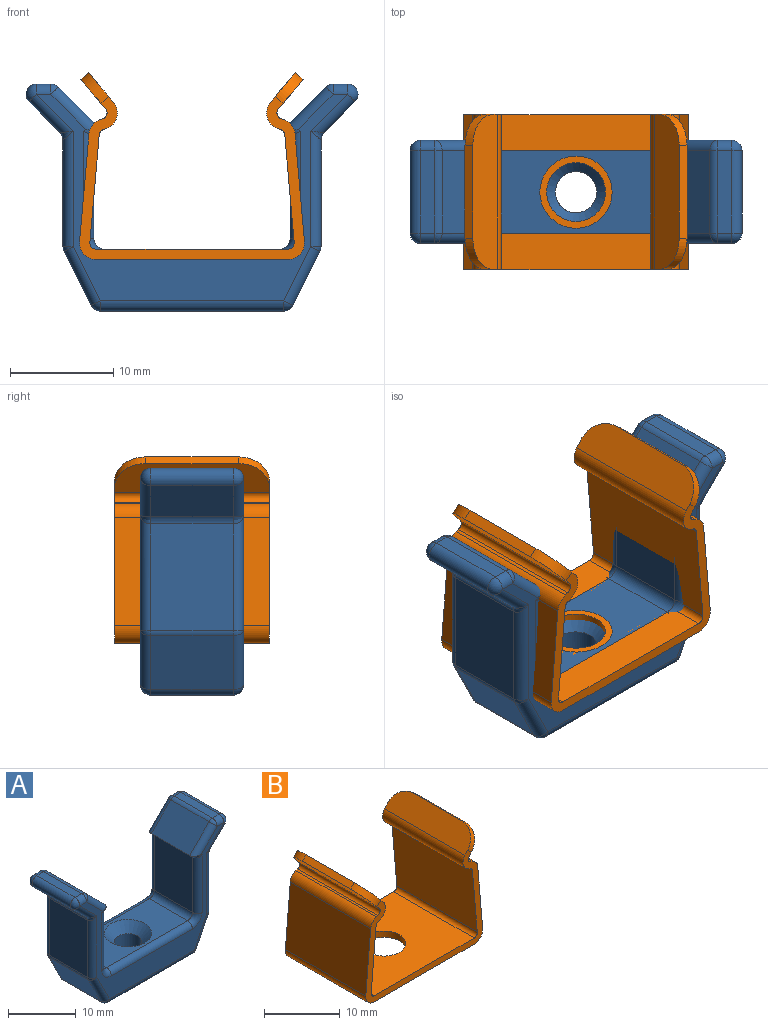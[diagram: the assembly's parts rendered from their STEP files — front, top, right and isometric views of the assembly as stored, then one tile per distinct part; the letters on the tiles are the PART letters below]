
ASSEMBLY  parts=2 mates=1
PART A: 88 faces, bbox 32.2x10x22 mm
  f0: plane 17x8mm, normal (0,0,1), area 97.5mm2, adj f27,f36,f37,f38,f69
  f1: plane 10x8mm, normal (1,0,0), area 80mm2, adj f2,f26,f27,f28
  f2: plane 8x0.62mm, normal (0.71,0,-0.71), area 7mm2, adj f1,f3,f22,f23
  f3: plane 8x4.09mm, normal (0.71,0,0.71), area 46.2mm2, adj f2,f18,f19,f20
  f4: plane 8x1.41mm, normal (0,0,1), area 11.3mm2, adj f20,f25,f29,f30
  f5: plane 8x3mm, normal (-0.71,0,-0.71), area 33.9mm2, adj f30,f35,f39,f83
  f6: plane 10.35x8mm, normal (-1,0,0), area 82.8mm2, adj f40,f43,f77,f83
  f7: plane 8x5.24mm, normal (-0.89,0,-0.45), area 46.8mm2, adj f44,f47,f77,f80
  f8: plane 17.76x8mm, normal (0,0,-1), area 129.5mm2, adj f48,f51,f68,f71,f80
  f9: plane 8x5.24mm, normal (0.89,0,-0.45), area 46.8mm2, adj f52,f56,f71,f74
  f10: plane 10.35x8mm, normal (1,0,0), area 82.8mm2, adj f57,f60,f74,f86
  f11: plane 8x3mm, normal (0.71,0,-0.71), area 33.9mm2, adj f61,f64,f67,f86
  f12: plane 8x1.41mm, normal (0,0,1), area 11.3mm2, adj f54,f62,f63,f67
  f13: plane 8x4.09mm, normal (-0.71,0,0.71), area 46.2mm2, adj f14,f53,f54,f55
  f14: plane 8x0.62mm, normal (-0.71,0,-0.71), area 7mm2, adj f13,f15,f49,f50
  f15: plane 10x8mm, normal (-1,0,0), area 80mm2, adj f14,f37,f45,f46
  f16: plane 30.17x20mm, normal (0,-1,0), area 114.9mm2, adj f18,f22,f25,f26,f32,f35,f36,f40
  f17: plane 30.17x20mm, normal (0,1,0), area 114.9mm2, adj f19,f23,f28,f29,f33,f38,f39,f42
  f18: cylinder r=1mm len=4.79mm, axis (0.71,0,-0.71), area 8.5mm2, adj f3,f16,f21,f22
  f19: cylinder r=1mm len=4.79mm, axis (-0.71,0,0.71), area 8.5mm2, adj f3,f17,f23,f24
  f20: cylinder r=1mm len=8mm, axis (0,1,0), area 6.3mm2, adj f3,f4,f21,f24
  f21: sphere r=1mm, area 0.8mm2, adj f18,f20,f25
  f22: cylinder r=1mm len=1.62mm, axis (-0.71,0,-0.71), area 1mm2, adj f2,f16,f18,f26
  f23: cylinder r=1mm len=1.62mm, axis (0.71,0,0.71), area 1mm2, adj f2,f17,f19,f28
  f24: sphere r=1mm, area 0.8mm2, adj f19,f20,f29
  f25: cylinder r=1mm len=1.41mm, axis (1,0,0), area 2.2mm2, adj f4,f16,f21,f31
  f26: cylinder r=1mm len=10.41mm, axis (0,0,-1), area 15.9mm2, adj f1,f16,f22,f32
  f27: cylinder r=1mm len=8mm, axis (0,1,0), area 12.6mm2, adj f0,f1,f32,f33
  f28: cylinder r=1mm len=10.41mm, axis (0,0,1), area 15.9mm2, adj f1,f17,f23,f33
  f29: cylinder r=1mm len=1.41mm, axis (-1,0,0), area 2.2mm2, adj f4,f17,f24,f34
  f30: cylinder r=1mm len=8mm, axis (0,1,0), area 18.8mm2, adj f4,f5,f31,f34
  f31: sphere r=1mm, area 2.4mm2, adj f25,f30,f35
  f32: torus R=2mm, axis (0,-1,0), area 3.4mm2, adj f16,f26,f27,f36
  f33: torus R=2mm, axis (0,-1,0), area 3.4mm2, adj f17,f27,f28,f38
  f34: sphere r=1mm, area 2.4mm2, adj f29,f30,f39
  f35: cylinder r=1mm len=4.29mm, axis (-0.71,0,0.71), area 7.1mm2, adj f5,f16,f31,f84
  f36: cylinder r=1mm len=17mm, axis (1,0,0), area 26.7mm2, adj f0,f16,f32,f41
  f37: cylinder r=1mm len=8mm, axis (0,-1,0), area 12.6mm2, adj f0,f15,f41,f42
  f38: cylinder r=1mm len=17mm, axis (-1,0,0), area 26.7mm2, adj f0,f17,f33,f42
  f39: cylinder r=1mm len=4.29mm, axis (0.71,0,-0.71), area 7.1mm2, adj f5,f17,f34,f82
  f40: cylinder r=1mm len=11.18mm, axis (0,0,1), area 16.7mm2, adj f6,f16,f78,f84
  f41: torus R=2mm, axis (0,-1,0), area 3.4mm2, adj f16,f36,f37,f45
  f42: torus R=2mm, axis (0,-1,0), area 3.4mm2, adj f17,f37,f38,f46
  f43: cylinder r=1mm len=11.18mm, axis (0,0,-1), area 16.7mm2, adj f6,f17,f76,f82
  f44: cylinder r=1mm len=5.68mm, axis (-0.45,0,0.89), area 9.2mm2, adj f7,f16,f78,f81
  f45: cylinder r=1mm len=10.41mm, axis (0,0,1), area 15.9mm2, adj f15,f16,f41,f49
  f46: cylinder r=1mm len=10.41mm, axis (0,0,-1), area 15.9mm2, adj f15,f17,f42,f50
  f47: cylinder r=1mm len=5.68mm, axis (0.45,0,-0.89), area 9.2mm2, adj f7,f17,f76,f79
  f48: cylinder r=1mm len=17.76mm, axis (-1,0,0), area 27.9mm2, adj f8,f16,f72,f81
  f49: cylinder r=1mm len=1.62mm, axis (-0.71,0,0.71), area 1mm2, adj f14,f16,f45,f53
  f50: cylinder r=1mm len=1.62mm, axis (0.71,0,-0.71), area 1mm2, adj f14,f17,f46,f55
  f51: cylinder r=1mm len=17.76mm, axis (1,0,0), area 27.9mm2, adj f8,f17,f70,f79
  f52: cylinder r=1mm len=5.68mm, axis (-0.45,0,-0.89), area 9.2mm2, adj f9,f16,f72,f75
  f53: cylinder r=1mm len=4.79mm, axis (0.71,0,0.71), area 8.5mm2, adj f13,f16,f49,f58
  f54: cylinder r=1mm len=8mm, axis (0,1,0), area 6.3mm2, adj f12,f13,f58,f59
  f55: cylinder r=1mm len=4.79mm, axis (-0.71,0,-0.71), area 8.5mm2, adj f13,f17,f50,f59
  f56: cylinder r=1mm len=5.68mm, axis (0.45,0,0.89), area 9.2mm2, adj f9,f17,f70,f73
  f57: cylinder r=1mm len=11.18mm, axis (0,0,-1), area 16.7mm2, adj f10,f16,f75,f87
  f58: sphere r=1mm, area 0.8mm2, adj f53,f54,f62
  f59: sphere r=1mm, area 0.8mm2, adj f54,f55,f63
  f60: cylinder r=1mm len=11.18mm, axis (0,0,1), area 16.7mm2, adj f10,f17,f73,f85
  f61: cylinder r=1mm len=4.29mm, axis (-0.71,0,-0.71), area 7.1mm2, adj f11,f16,f65,f87
  f62: cylinder r=1mm len=1.41mm, axis (1,0,0), area 2.2mm2, adj f12,f16,f58,f65
  f63: cylinder r=1mm len=1.41mm, axis (-1,0,0), area 2.2mm2, adj f12,f17,f59,f66
  f64: cylinder r=1mm len=4.29mm, axis (0.71,0,0.71), area 7.1mm2, adj f11,f17,f66,f85
  f65: sphere r=1mm, area 2.4mm2, adj f61,f62,f67
  f66: sphere r=1mm, area 2.4mm2, adj f63,f64,f67
  f67: cylinder r=1mm len=8mm, axis (0,1,0), area 18.8mm2, adj f11,f12,f65,f66
  f68: cylinder r=2mm len=4.5mm, axis (0,0,1), area 56.5mm2, adj f8,f69
  f69: cone r=2mm half-angle=45deg, axis (0,0,1), area 36.7mm2, adj f0,f68
  f70: sphere r=1mm, area 1.1mm2, adj f51,f56,f71
  f71: cylinder r=1mm len=8mm, axis (0,-1,0), area 8.9mm2, adj f8,f9,f70,f72
  f72: sphere r=1mm, area 1.1mm2, adj f48,f52,f71
  f73: sphere r=1mm, area 0.5mm2, adj f56,f60,f74
  f74: cylinder r=1mm len=8mm, axis (0,1,0), area 3.7mm2, adj f9,f10,f73,f75
  f75: sphere r=1mm, area 0.5mm2, adj f52,f57,f74
  f76: sphere r=1mm, area 0.5mm2, adj f43,f47,f77
  f77: cylinder r=1mm len=8mm, axis (0,1,0), area 3.7mm2, adj f6,f7,f76,f78
  f78: sphere r=1mm, area 0.5mm2, adj f40,f44,f77
  f79: sphere r=1mm, area 1.1mm2, adj f47,f51,f80
  f80: cylinder r=1mm len=8mm, axis (0,1,0), area 8.9mm2, adj f7,f8,f79,f81
  f81: sphere r=1mm, area 1.1mm2, adj f44,f48,f80
  f82: bspline ~1.29x1.13mm, area 0.8mm2, adj f39,f43,f83
  f83: cylinder r=1mm len=8mm, axis (0,-1,0), area 6.3mm2, adj f5,f6,f82,f84
  f84: bspline ~1.29x1.13mm, area 0.8mm2, adj f35,f40,f83
  f85: bspline ~1.29x1.13mm, area 0.8mm2, adj f60,f64,f86
  f86: cylinder r=1mm len=8mm, axis (0,-1,0), area 6.3mm2, adj f10,f11,f85,f87
  f87: bspline ~1.29x1.13mm, area 0.8mm2, adj f57,f61,f86
PART B: 35 faces, bbox 21.8x15x18.1 mm
  f0: plane 15x0.31mm, normal (-0.34,0,0.94), area 5mm2, adj f16,f17,f18,f29
  f1: plane 15x10.42mm, normal (-1,0,0.09), area 156.9mm2, adj f16,f17,f18,f19
  f2: plane 18.61x15mm, normal (0,0,-1), area 253.6mm2, adj f16,f17,f19,f23,f34
  f3: plane 15x10.42mm, normal (1,0,0.09), area 156.9mm2, adj f16,f17,f20,f23
  f4: plane 15x0.31mm, normal (0.34,0,0.94), area 5mm2, adj f16,f17,f20,f24
  f5: plane 15x2.85mm, normal (0.77,0,-0.64), area 51.9mm2, adj f6,f16,f17,f24,f31,f33
  f6: plane 9x0.77mm, normal (0.64,0,0.77), area 9mm2, adj f5,f7,f31,f33
  f7: plane 15x2.85mm, normal (-0.77,0,0.64), area 51.9mm2, adj f6,f16,f17,f21,f31,f33
  f8: plane 15x0.31mm, normal (-0.34,0,-0.94), area 5mm2, adj f16,f17,f21,f25
  f9: plane 15x10.42mm, normal (-1,0,-0.09), area 156.9mm2, adj f16,f17,f25,f26
  f10: plane 18.61x15mm, normal (0,0,1), area 253.6mm2, adj f16,f17,f26,f27,f34
  f11: plane 15x10.42mm, normal (1,0,-0.09), area 156.9mm2, adj f16,f17,f27,f28
  f12: plane 15x0.31mm, normal (0.34,0,-0.94), area 5mm2, adj f16,f17,f22,f28
  f13: plane 15x2.85mm, normal (0.77,0,0.64), area 51.9mm2, adj f14,f16,f17,f22,f30,f32
  f14: plane 9x0.77mm, normal (-0.64,0,0.77), area 9mm2, adj f13,f15,f30,f32
  f15: plane 15x2.85mm, normal (-0.77,0,-0.64), area 51.9mm2, adj f14,f16,f17,f29,f30,f32
  f16: plane 21.81x15.78mm, normal (0,-1,0), area 52mm2, adj f0,f1,f2,f3,f4,f5,f7,f8
  f17: plane 21.81x15.78mm, normal (0,1,0), area 52mm2, adj f0,f1,f2,f3,f4,f5,f7,f8
  f18: cylinder r=1.6mm len=15mm, axis (0,1,0), area 27.2mm2, adj f0,f1,f16,f17
  f19: cylinder r=1.6mm len=15mm, axis (0,1,0), area 39.8mm2, adj f1,f2,f16,f17
  f20: cylinder r=1.6mm len=15mm, axis (0,-1,0), area 27.2mm2, adj f3,f4,f16,f17
  f21: cylinder r=1.6mm len=15mm, axis (0,1,0), area 46.1mm2, adj f7,f8,f16,f17
  f22: cylinder r=1.6mm len=15mm, axis (0,1,0), area 46.1mm2, adj f12,f13,f16,f17
  f23: cylinder r=1.6mm len=15mm, axis (0,-1,0), area 39.8mm2, adj f2,f3,f16,f17
  f24: cylinder r=0.6mm len=15mm, axis (0,1,0), area 17.3mm2, adj f4,f5,f16,f17
  f25: cylinder r=0.6mm len=15mm, axis (0,-1,0), area 10.2mm2, adj f8,f9,f16,f17
  f26: cylinder r=0.6mm len=15mm, axis (0,-1,0), area 14.9mm2, adj f9,f10,f16,f17
  f27: cylinder r=0.6mm len=15mm, axis (0,1,0), area 14.9mm2, adj f10,f11,f16,f17
  f28: cylinder r=0.6mm len=15mm, axis (0,-1,0), area 10.2mm2, adj f11,f12,f16,f17
  f29: cylinder r=0.6mm len=15mm, axis (0,-1,0), area 17.3mm2, adj f0,f15,f16,f17
  f30: cylinder r=3mm len=3mm, axis (-0.77,0,-0.64), area 4.7mm2, adj f13,f14,f15,f17
  f31: cylinder r=3mm len=3mm, axis (-0.77,0,0.64), area 4.7mm2, adj f5,f6,f7,f17
  f32: cylinder r=3mm len=3mm, axis (0.77,0,0.64), area 4.7mm2, adj f13,f14,f15,f16
  f33: cylinder r=3mm len=3mm, axis (0.77,0,-0.64), area 4.7mm2, adj f5,f6,f7,f16
  f34: cylinder r=2.85mm len=5.7mm, axis (0,0,-1), area 17.9mm2, adj f2,f10
PLACE A at identity
PLACE B t=(-10.04,2.5,-6.5)mm
MATE revolute B.f34 <-> A.f68  axis (0,0,1) through (0,-5,-5.5)mm
